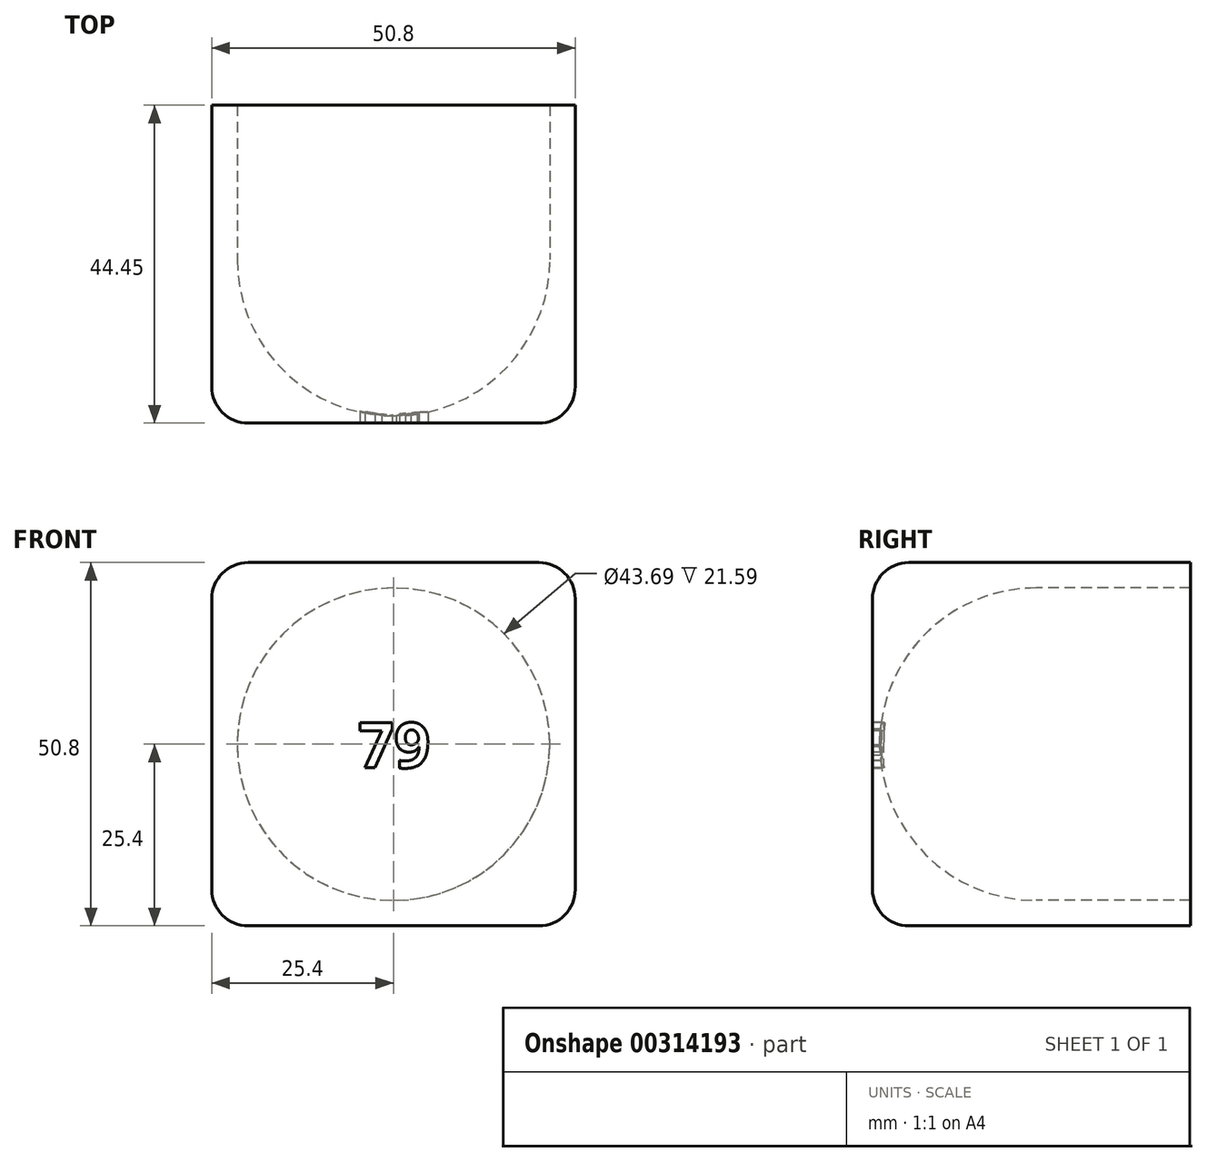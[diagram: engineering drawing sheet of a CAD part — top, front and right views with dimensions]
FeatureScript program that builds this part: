
annotation { "Feature Type Name" : "Feature", "Feature Type Description" : "" }
export const myFeature = defineFeature(function(context is Context, id is Id, definition is map)
    precondition{}
    {
        {
            var Q0;
            Q0=qCreatedBy(makeId("Front.planeOp"),FACE);
            var sketch = newSketch(context, id + "F0", { "sketchPlane" : qUnion([Q0])});
            skCircle(sketch, "E0", {"center": v(0, 0) * mm, "radius": 21.59 * mm});
            skLineSegment(sketch, "E1.bottom", {"start": v(25.4, -25.4) * mm, "end": v(-25.4, -25.4) * mm});
            skLineSegment(sketch, "E1.top", {"start": v(25.4, 25.4) * mm, "end": v(-25.4, 25.4) * mm});
            skLineSegment(sketch, "E1.left", {"start": v(25.4, -25.4) * mm, "end": v(25.4, 25.4) * mm});
            skLineSegment(sketch, "E1.right", {"start": v(-25.4, -25.4) * mm, "end": v(-25.4, 25.4) * mm});
            skSolve(sketch);
        }
        {
            var Q0;
            Q0=makeQuery(id+"F0.imprint","IMPRINT",FACE,{"disambiguationData":[TD([[makeQuery(id+"F0.imprint","IMPRINT",EDGE,{"derivedFrom":sQuery(id+"F0.wireOp",EDGE,"E0")}),-1.0]])]});
            var Q1;
            Q1=makeQuery(id+"F0.imprint","IMPRINT",FACE,{"disambiguationData":[TD([[makeQuery(id+"F0.imprint","IMPRINT",EDGE,{"derivedFrom":sQuery(id+"F0.wireOp",EDGE,"E0")}),1.0]])]});
            extrude(context, id + "F1", {"entities" : qUnion([Q0, Q1]), "depth" : 22.86 * mm});
        }
        {
            var Q0;
            Q0=qCreatedBy(makeId("Right.planeOp"),FACE);
            var sketch = newSketch(context, id + "F2", { "sketchPlane" : qUnion([Q0])});
            skLineSegment(sketch, "E2", {"start": v(0, 0) * mm, "end": v(-21.84, 0) * mm});
            skPoint(sketch, "E3.end.orphan", {"position": v(0, -21.84) * mm});
            skArc(sketch, "E4", {"start": v(0, -21.84) * mm, "mid": v(-15.45, -15.45) * mm, "end": v(-21.84, 0) * mm});
            skLineSegment(sketch, "E5", {"start": v(0, 0) * mm, "end": v(0, -21.84) * mm});
            skSolve(sketch);
        }
        {
            var Q0;
            Q0 = qSketchRegion(id + "F2", true);
            var Q1;
            Q1=sQuery(id+"F2.wireOp",EDGE,"E2");
            revolve(context, id + "F3", {"operationType" : NewBodyOperationType.REMOVE, "entities" : qUnion([Q0]), "axis" : qUnion([Q1]), "revolveType" : RevolveType.FULL, "oppositeDirection" : true});
        }
        {
            var Q0;
            Q0=makeQuery(id+"F1.opExtrude","CAP_FACE",FACE,{"disambiguationData":[OSD([sQuery(id+"F0.wireOp",EDGE,"E1.bottom"),sQuery(id+"F0.wireOp",EDGE,"E1.top"),sQuery(id+"F0.wireOp",EDGE,"E1.left"),sQuery(id+"F0.wireOp",EDGE,"E1.right")])],"isStart":false});
            var Q1;
            Q1=makeQuery(id+"F1.opExtrude","SWEPT_EDGE",EDGE,{"disambiguationData":[OSD([sQuery(id+"F0.wireOp",EDGE,"E1.top"),sQuery(id+"F0.wireOp",EDGE,"E1.right")])]});
            var Q2;
            Q2=makeQuery(id+"F1.opExtrude","SWEPT_EDGE",EDGE,{"disambiguationData":[OSD([sQuery(id+"F0.wireOp",EDGE,"E1.top"),sQuery(id+"F0.wireOp",EDGE,"E1.left")])]});
            var Q3;
            Q3=makeQuery(id+"F1.opExtrude","SWEPT_EDGE",EDGE,{"disambiguationData":[OSD([sQuery(id+"F0.wireOp",EDGE,"E1.bottom"),sQuery(id+"F0.wireOp",EDGE,"E1.right")])]});
            var Q4;
            Q4=makeQuery(id+"F1.opExtrude","SWEPT_EDGE",EDGE,{"disambiguationData":[OSD([sQuery(id+"F0.wireOp",EDGE,"E1.bottom"),sQuery(id+"F0.wireOp",EDGE,"E1.left")])]});
            fillet(context, id + "F4", {"entities" : qUnion([Q0, Q1, Q2, Q3, Q4]), "radius" : 5.08 * mm, "tangentPropagation" : true, "allowEdgeOverflow" : false});
        }
        {
            var Q0;
            Q0=makeQuery(id+"F1.opExtrude","CAP_FACE",FACE,{"disambiguationData":[OSD([sQuery(id+"F0.wireOp",EDGE,"E1.bottom"),sQuery(id+"F0.wireOp",EDGE,"E1.top"),sQuery(id+"F0.wireOp",EDGE,"E1.left"),sQuery(id+"F0.wireOp",EDGE,"E1.right")])],"isStart":false});
            var sketch = newSketch(context, id + "F5", { "sketchPlane" : qUnion([Q0])});
            skText(sketch, "E6", { "text": "79", "fontName": "OpenSans-Bold.ttf"});
            const initialGuessF5  = {"E6": [-0.00495, -0.0033, 1, 0, 0.00635]};
            skSetInitialGuess(sketch, initialGuessF5);
            skSolve(sketch);
        }
        {
            var Q0;
            Q0 = qSketchRegion(id + "F5", true);
            extrude(context, id + "F6", {"entities" : qUnion([Q0]), "operationType" : NewBodyOperationType.REMOVE, "oppositeDirection" : true, "depth" : 25.4 * mm});
        }
        {
            var Q0;
            Q0=makeQuery(id+"F1.opExtrude","CAP_FACE",FACE,{"disambiguationData":[OSD([sQuery(id+"F0.wireOp",EDGE,"E1.bottom"),sQuery(id+"F0.wireOp",EDGE,"E1.top"),sQuery(id+"F0.wireOp",EDGE,"E1.left"),sQuery(id+"F0.wireOp",EDGE,"E1.right")])],"isStart":true});
            var sketch = newSketch(context, id + "F7", { "sketchPlane" : qUnion([Q0])});
            skSolve(sketch);
        }
        {
            var Q0;
            {var subQ3=sQuery(id+"F0.wireOp",EDGE,"E1.bottom");Q0=makeQuery(id+"F7.imprint","IMPRINT",FACE,{"disambiguationData":[TD([[makeQuery(id+"F7.imprint","IMPRINT",EDGE,{"derivedFrom":makeQuery(id+"F1.opExtrude","CAP_EDGE",EDGE,{"disambiguationData":[OSD([subQ3])],"isStart":true})}),1.0]])]});}
            extrude(context, id + "F8", {"entities" : qUnion([Q0]), "operationType" : NewBodyOperationType.ADD, "depth" : 21.59 * mm});
        }
    });
